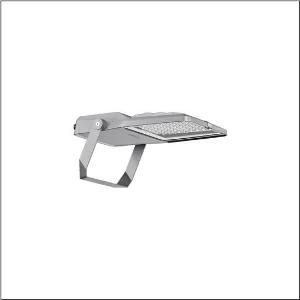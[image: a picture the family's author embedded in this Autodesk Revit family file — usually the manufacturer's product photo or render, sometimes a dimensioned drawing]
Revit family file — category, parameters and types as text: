
# Revit family: floodlight_fl_21_iq_mini___pl64_5xa7771c2e1a_63e9
name_source: partatom
category: Lighting Fixtures
units: mm (PartAtom-declared; Revit-internal decimal feet)

## family parameters
Cut with Voids When Loaded = No
Host = Face
Light Source = No
Part Type = Normal
Room Calculation Point = No
Round Connector Dimension = Use Diameter
Shared = No

## types (1)
- --- (1 x LED, 11790 lm, 87.2 W, 3000K)
    Apparent Load = 87 VA
    CIE Flux Codes = 28 80 98 100 100
    Color Rendering = 70
    Color Temperature = 3000K
    Default Elevation = 1800 mm
    Description = Floodlight FL 21 iQ mini, floodlight, primary light control with lens, of PMMA, primary optical cover: protective disc, of toughened safety glass, transparent, light distribution: PL64, light emission: direct distribution, installation type: surface-mounted, LED, High Power LED, rated luminous flux: 11.790lm, luminous efficacy: 135lm/W, light colour: 730, colour temperature: 3000K, control: Auto-Match, Temp-Guard, Lumen-Switch, Night-Set, Smart-Wire, Light-Fading, Desk-Remote (wireless, voltage-free reading and setting of iQ features in the workshop via application-optimized NFC function/RFID function), optimised constant luminous flux control (CLO 2.0), with terminal, 6-pole, mains connection: 220..240V, AC, 50/60Hz, start of lifetime: 87W, end of service life: 92W, reduction: 40W, luminaire housing, of diecast aluminium, powder-coated, Siteco® metallic grey (DB 702S), corrosivity category C5 mid according to DIN EN ISO 12944, sealing non-destructively replaceable, mounting bracket, of steel, galvanised, powder-coated, Siteco® metallic grey (DB 702S), protection rating (complete): IP66, insulation class (complete): insulation class II (safety insulation), certification: CE, ENEC, VDE, protection symbol: D, impact resistance: IK08, permissible operating ambient temperature: -40..+40°C, permissible operating ambient temperature for outdoor applications: -40..+50°C, standard: DIN EN 12944, LABS conformity tested according to VDMA 24364:2018-05, packaging unit: 1 piece

Light Distribution: PL64
    Height = 70 mm
    Lamp = 1 x LED
    Lamp Light Flux = 11790 lm
    Lamp Power = 87.2 W
    Lamp count = 1
    Length = 485 mm
    Luminous efficacy = 135 lm/W
    Manufacturer = Siteco
    ModVariant = No
    Model = 5XA7771C2E1A
    Number of Poles = 1
    OnlyDefault = Yes
    Power Factor = 1
    Product Name = Floodlight FL 21 iQ mini | PL64
    Product group = floodlight | pylon annexe
    ProductGroupID = 6200
    Protection Class = Protection class II
    Protection Degree = IP 66
    RLX_Detail_Level = 1
    RLX_Emergency_Light_Flux = 0 lm
    RLX_Emergency_Type = 0
    RLX_Emergency_Type_DB = No
    RlxData = <blob elided: 96229 chars, md5=1845ccba>
    Socket = socket
    Standby Power = 0 W
    System Light Flux = 11790 lm
    System Power = 87 W
    Type Comments = factory setting: luminous flux: 100 % | dim-lin: 254 | 456 mA
    Type Image = l_1006845.jpg
    URL = http://relux.com
    VarID = @adj_116837
    Voltage = 0 V
    Weight = 0.00 kg
    Width = 337 mm

## geometry (parser evidence)
native form markers: Blend x4, Sweep x12
no freeform markers — native parametric forms only
